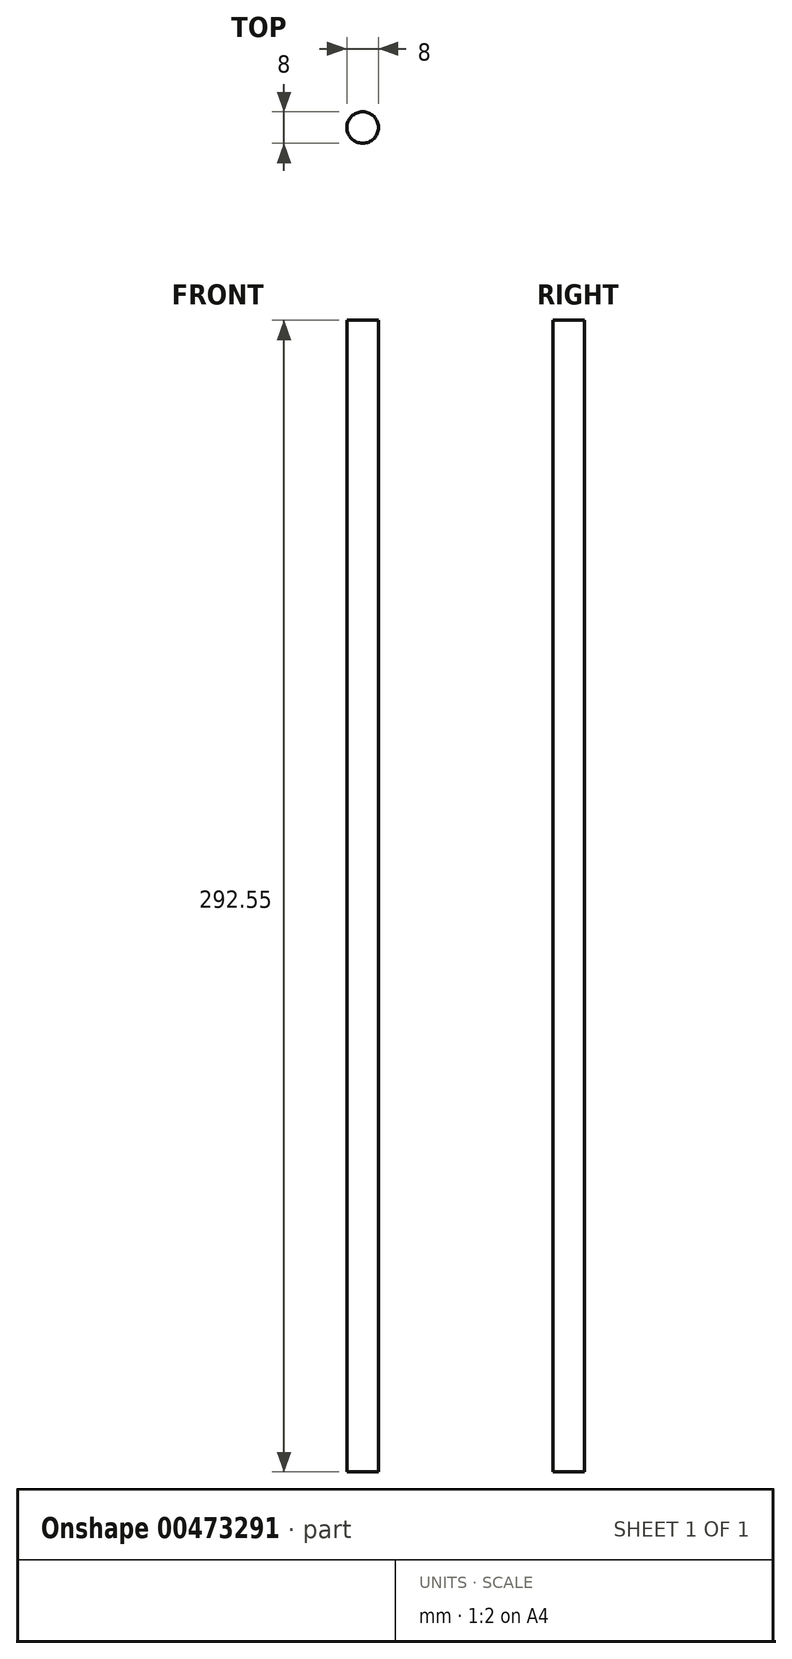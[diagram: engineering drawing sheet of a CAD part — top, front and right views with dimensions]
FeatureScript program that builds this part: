
annotation { "Feature Type Name" : "Feature", "Feature Type Description" : "" }
export const myFeature = defineFeature(function(context is Context, id is Id, definition is map)
    precondition{}
    {
        {
            var Q0;
            Q0=qCreatedBy(makeId("Top.planeOp"),FACE);
            var sketch = newSketch(context, id + "F0", { "sketchPlane" : qUnion([Q0])});
            skCircle(sketch, "E0", {"center": v(0, 0) * mm, "radius": 4 * mm});
            skSolve(sketch);
        }
        {
            var Q0;
            Q0 = qSketchRegion(id + "F0", true);
            extrude(context, id + "F1", {"entities" : qUnion([Q0]), "depth" : 292.55 * mm, "offsetDistance" : 25 * mm});
        }
    });
